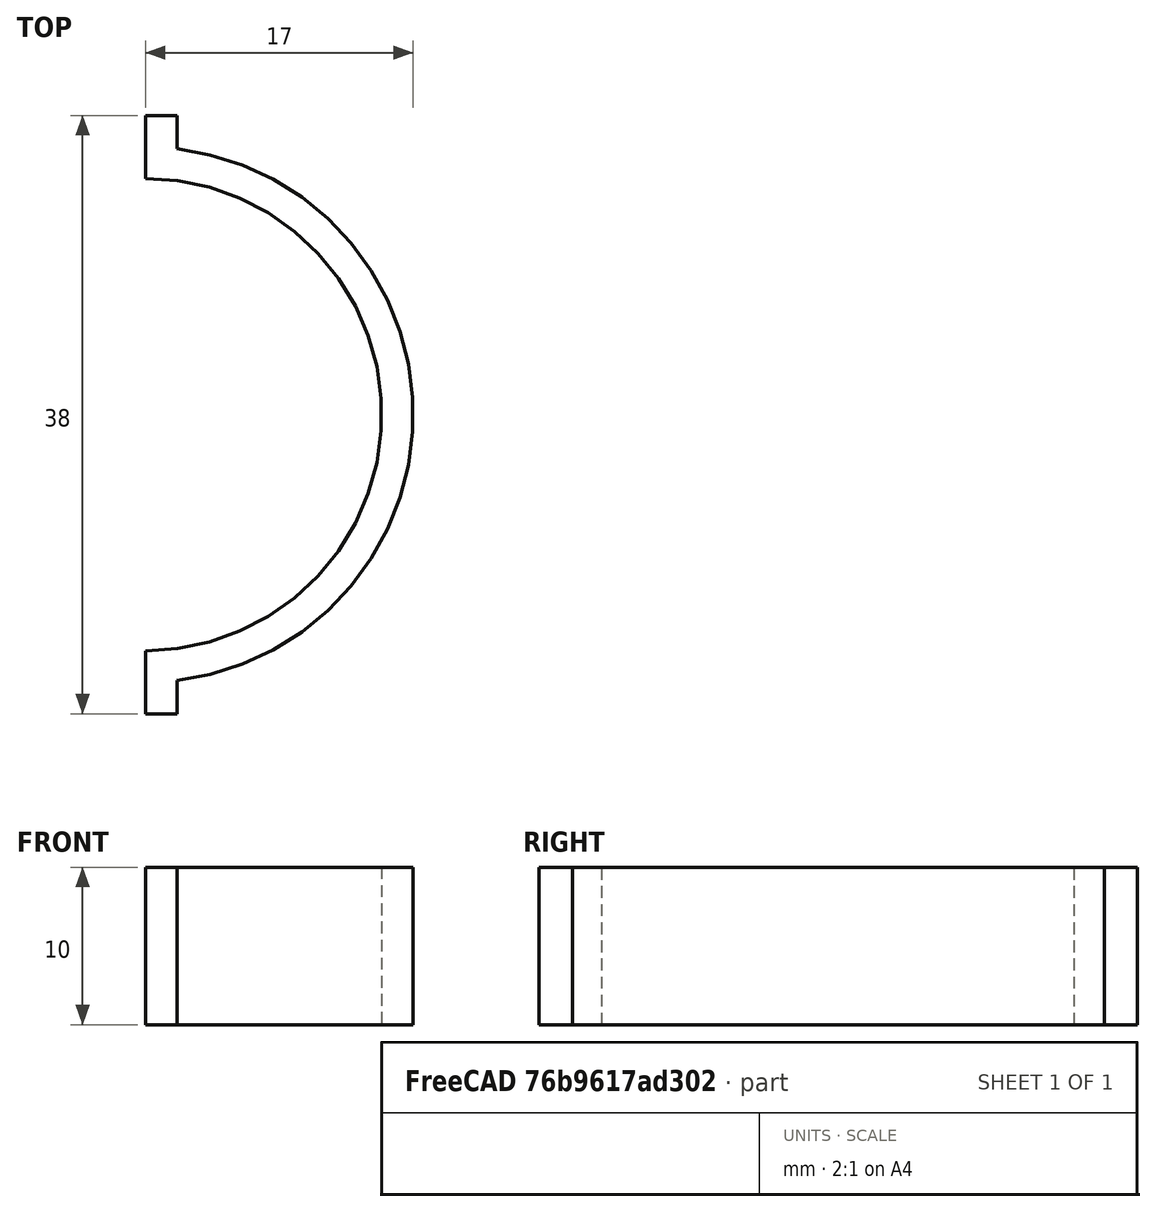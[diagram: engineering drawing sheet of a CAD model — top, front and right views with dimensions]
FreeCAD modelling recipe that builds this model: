
FCSTD DOCUMENT  (FreeCAD 2023.131R26244 +5365 (Git))
Label: Bike Thing 2
License: All rights reserved
LicenseURL: http://en.wikipedia.org/wiki/All_rights_reserved
objects: Spreadsheet::Sheet×1, Sketcher::SketchObject×1, PartDesign::Pad×1, PartDesign::Body×1
note: 6 computed .brp shape members not serialized (recipe doc carries the construction recipe); baked Part::Feature solids carry a one-line shape summary decoded from their .brp

FEATURE [Spreadsheet::Sheet] Spreadsheet  label="Parameters"
  PythonMode = false
  ShowCells = 0
  TreeRank = 1
  cells = A1=Thickness; B1(Thickness)=2; A2=Bar Dimension 1; B2(Bar_Dimension_1)=30; A3=Bar Dimension 2; B3(Bar_Dimension_2)=35
FEATURE [Sketcher::SketchObject] Sketch
  ArcFitTolerance = 1e-06
  AttachmentSupport = -> [XY_Plane]
  ExternalBSplineMaxDegree = 5
  ExternalBSplineTolerance = 0.0001
  FullyConstrained = false
  InternalTolerance = 1e-06
  InvalidShape = false
  MakeInternals = false
  MapMode = 5
  Support = -> [XY_Plane]
  TreeRank = 12
  ValidateShape = true
  expr: Constraints[16] = <<Parameters>>.Thickness
  expr: Constraints[20] = <<Parameters>>.Thickness
  expr: Constraints[22] = <<Parameters>>.Thickness
  expr: Constraints[2] = <<Parameters>>.Thickness * 2
  expr: Constraints[6] = <<Parameters>>.Bar_Dimension_1 / 2
  sketch-geometry (17):
    g0: LineSegment StartX=0 StartY=15 StartZ=0 EndX=0 EndY=19 EndZ=0
    g1: LineSegment StartX=0 StartY=-15 StartZ=0 EndX=0 EndY=-19 EndZ=0
    g2: ArcOfEllipse CenterX=0 CenterY=0 CenterZ=0 NormalX=0 NormalY=0 NormalZ=1 MajorRadius=15 MinorRadius=15 AngleXU=0 StartAngle=4.71239 EndAngle=7.85398
    g3: LineSegment [constr] StartX=15 StartY=0 StartZ=0 EndX=-15 EndY=0 EndZ=0
    g4: GeomPoint [constr] X=1.11819e-06 Y=0 Z=0
    g5: GeomPoint [constr] X=-1.11819e-06 Y=0 Z=0
    g6: LineSegment StartX=0 StartY=19 StartZ=0 EndX=2 EndY=19 EndZ=0
    g7: LineSegment StartX=0 StartY=-19 StartZ=0 EndX=2 EndY=-19 EndZ=0
    g8: GeomPoint [constr] X=0 Y=-17 Z=0
    g9: GeomPoint [constr] X=0 Y=17 Z=0
    g10: ArcOfEllipse CenterX=0 CenterY=0 CenterZ=0 NormalX=0 NormalY=0 NormalZ=1 MajorRadius=17 MinorRadius=17 AngleXU=0 StartAngle=4.83031 EndAngle=7.73606
    g11: LineSegment [constr] StartX=17 StartY=0 StartZ=0 EndX=-17 EndY=0 EndZ=0
    g12: LineSegment [constr] StartX=0 StartY=17 StartZ=0 EndX=0 EndY=-17 EndZ=0
    g13: GeomPoint [constr] X=1.20989e-06 Y=0 Z=0
    g14: GeomPoint [constr] X=-1.20989e-06 Y=0 Z=0
    g15: LineSegment StartX=2 StartY=-19 StartZ=0 EndX=2 EndY=-16.8819 EndZ=0
    g16: LineSegment StartX=2 StartY=19 StartZ=0 EndX=2 EndY=16.8819 EndZ=0
  constraints (34):
    c: PointOnObject(g0,g-2)
    c: PointOnObject(g0,g-2)
    c: Distance(g0,g0) = 4
    c: PointOnObject(g1,g-2)
    c: PointOnObject(g1,g-2)
    c: Equal(g0,g1)
    c: DistanceY(g-1,g0) = 15
    c: InternalAlignment(g3,g2)
    c: InternalAlignment(g4,g2)
    c: InternalAlignment(g5,g2)
    c: Coincident(g2,g-1)
    c: Coincident(g2,g0)
    c: Coincident(g6,g0)
    c: Horizontal(g6)
    c: Coincident(g7,g1)
    c: Horizontal(g7)
    c: Distance(g7) = 2
    c: Equal(g7,g6)
    c: PointOnObject(g8,g1)
    c: Coincident(g2,g1)
    c: Distance(g1,g8) = 2
    c: PointOnObject(g9,g0)
    c: Distance(g0,g9) = 2
    c: PointOnObject(g3,g-1)
    c: InternalAlignment(g11-g14 -> g10) x4
    c: Coincident(g10,g2)
    c: PointOnObject(g9,g10)
    c: PointOnObject(g11,g-1)
    c: Coincident(g15,g7)
    c: Vertical(g15)
    c: Coincident(g16,g6)
    c: Vertical(g16)
    c: Coincident(g10,g16)
    c: Coincident(g10,g15)
FEATURE [PartDesign::Pad] Pad
  AddSubType = 0
  AlongSketchNormal = false
  AutoTaperInnerAngle = true
  CheckUpToFaceLimits = true
  ClaimChildren = false
  Direction = (0,0,1)
  Fit = 0
  FitJoin = 0
  InnerFit = 0
  InnerFitJoin = 0
  InvalidShape = false
  Length = 10
  Length2 = 100
  Linearize = true
  NewSolid = false
  Profile = -> Sketch
  Suppress = false
  TaperInnerAngle = 0
  TaperInnerAngleRev = 0
  TreeRank = 13
  Type = 0
  ValidateShape = true
  _ProfileBasedVersion = 1
FEATURE [PartDesign::Body] Body
  AutoGroupSolids = false
  ClaimAllChildren = false
  ExportMode = 0
  Group = -> [Sketch,Pad]
  InvalidShape = false
  Origin = -> Origin
  Tip = -> Pad
  TreeRank = 11
  ValidateShape = true
  _ExportChildren = -> [Pad]
  _GroupVersion = 1
